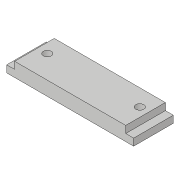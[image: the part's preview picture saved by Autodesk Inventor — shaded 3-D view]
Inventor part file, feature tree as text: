
AUTODESK INVENTOR PART (.ipt)
format: ipt  version: 2018.3 (Build 223284000, 284)  size: 102,912 bytes
history: native  units: in
note: dims shown in document units (in); Inventor stores cm internally (conversion verified against a paired STEP export)
features: extrude x3, sketch x3
ambient origin geometry x8: Origin, YZ Plane, XZ Plane, XY Plane, X Axis, Y Axis, Z Axis, Center Point
bodies: Solid1 (feature_tree)
feature tree (6):
  extrude  "Extrusion1"  Depth=0.625in
  extrude  "Extrusion6"  Depth=0.221in
  extrude  "Extrusion7"  Depth=0.1105in
  sketch  "Sketch1"  dims[d0=2.0in d1=0.625in]
  sketch  "Sketch7"  dims[d2=0.221in d3=0.0in d22=0.126in]
  sketch  "Sketch8"  dims[d23=0.126in d24=1.4567in d32=1.0in d33=0.0in d34=0.125in d35=0.125in d36=0.1105in d37=0.0in d42=0.2776in d43=0.2619in d44=0.2619in]
